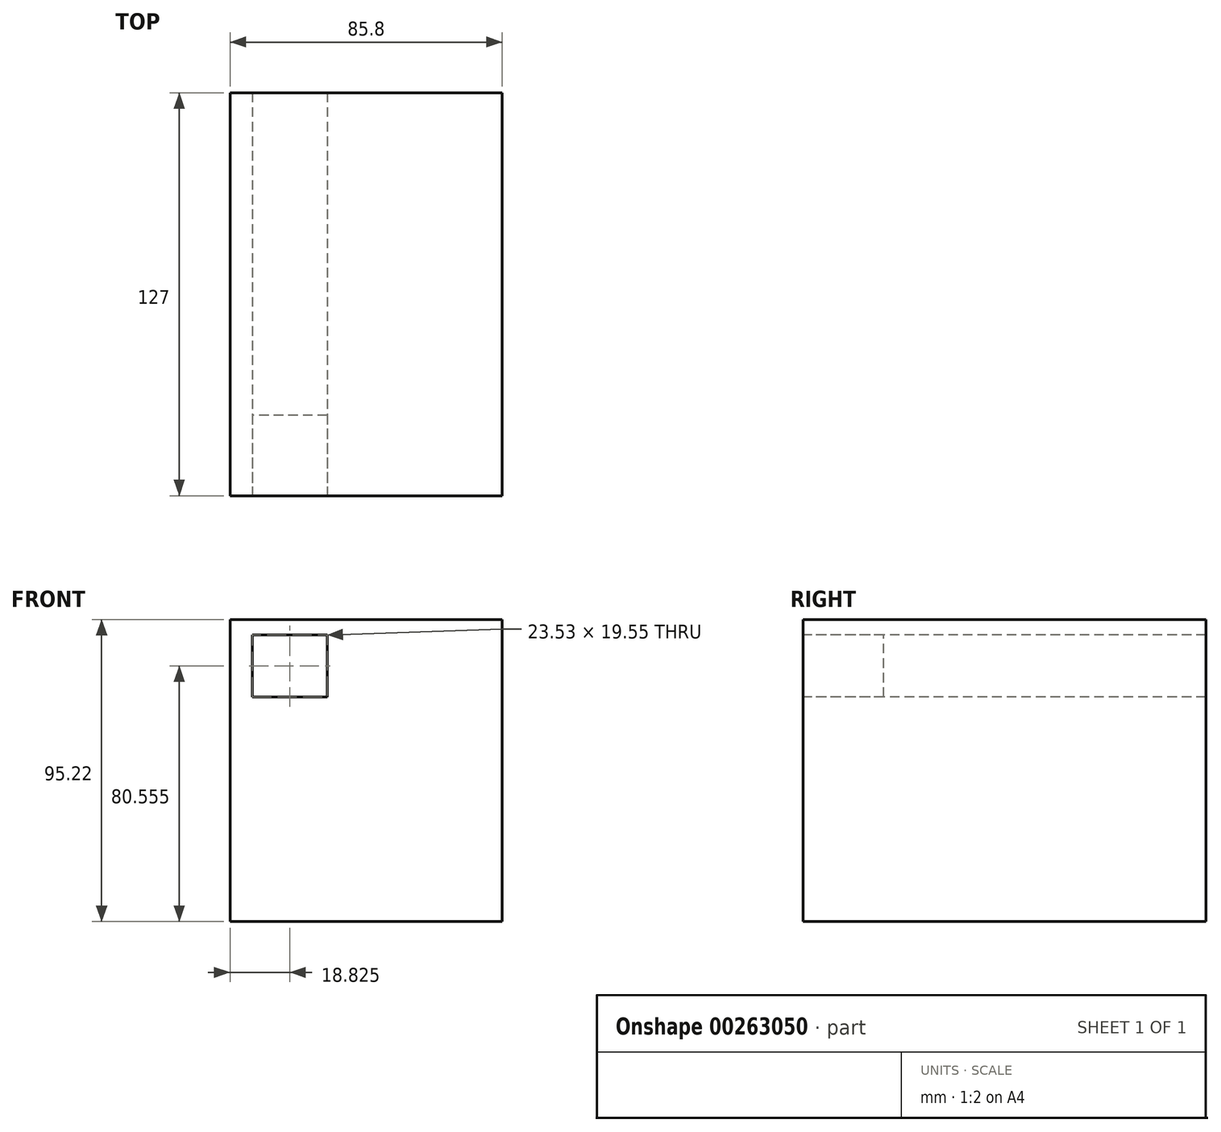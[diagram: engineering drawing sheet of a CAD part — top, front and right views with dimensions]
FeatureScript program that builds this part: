
annotation { "Feature Type Name" : "Feature", "Feature Type Description" : "" }
export const myFeature = defineFeature(function(context is Context, id is Id, definition is map)
    precondition{}
    {
        {
            var Q0;
            Q0=qCreatedBy(makeId("Front.planeOp"),FACE);
            var sketch = newSketch(context, id + "F0", { "sketchPlane" : qUnion([Q0])});
            skLineSegment(sketch, "E0.bottom", {"start": v(42.9, 47.6) * mm, "end": v(-42.9, 47.6) * mm});
            skLineSegment(sketch, "E0.top", {"start": v(42.9, -47.6) * mm, "end": v(-42.9, -47.6) * mm});
            skLineSegment(sketch, "E0.left", {"start": v(42.9, 47.6) * mm, "end": v(42.9, -47.6) * mm});
            skLineSegment(sketch, "E0.right", {"start": v(-42.9, 47.6) * mm, "end": v(-42.9, -47.6) * mm});
            skPoint(sketch, "E0.middle", {"position": v(0, 0) * mm});
            skSolve(sketch);
        }
        {
            var Q0;
            Q0 = qSketchRegion(id + "F0", true);
            extrude(context, id + "F1", {"entities" : qUnion([Q0]), "depth" : 127 * mm});
        }
        {
            var Q0;
            Q0=makeQuery(id+"F1.opExtrude","CAP_FACE",FACE,{"disambiguationData":[OSD([sQuery(id+"F0.wireOp",EDGE,"E0.bottom"),sQuery(id+"F0.wireOp",EDGE,"E0.top"),sQuery(id+"F0.wireOp",EDGE,"E0.left"),sQuery(id+"F0.wireOp",EDGE,"E0.right")])],"isStart":false});
            var sketch = newSketch(context, id + "F2", { "sketchPlane" : qUnion([Q0])});
            skLineSegment(sketch, "E1.bottom", {"start": v(-12.3, 23.17) * mm, "end": v(-35.84, 23.17) * mm});
            skLineSegment(sketch, "E1.top", {"start": v(-12.3, 42.72) * mm, "end": v(-35.84, 42.72) * mm});
            skLineSegment(sketch, "E1.left", {"start": v(-12.3, 23.17) * mm, "end": v(-12.3, 42.72) * mm});
            skLineSegment(sketch, "E1.right", {"start": v(-35.84, 23.17) * mm, "end": v(-35.84, 42.72) * mm});
            skPoint(sketch, "E1.middle", {"position": v(-24.08, 32.95) * mm});
            skSolve(sketch);
        }
        {
            var Q0;
            Q0 = qSketchRegion(id + "F2", true);
            extrude(context, id + "F3", {"entities" : qUnion([Q0]), "operationType" : NewBodyOperationType.REMOVE, "oppositeDirection" : true, "depth" : 127 * mm});
        }
        {
            var Q0;
            Q0 = qSketchRegion(id + "F2", true);
            extrude(context, id + "F4", {"entities" : qUnion([Q0]), "oppositeDirection" : true, "depth" : 25.4 * mm});
        }
    });
